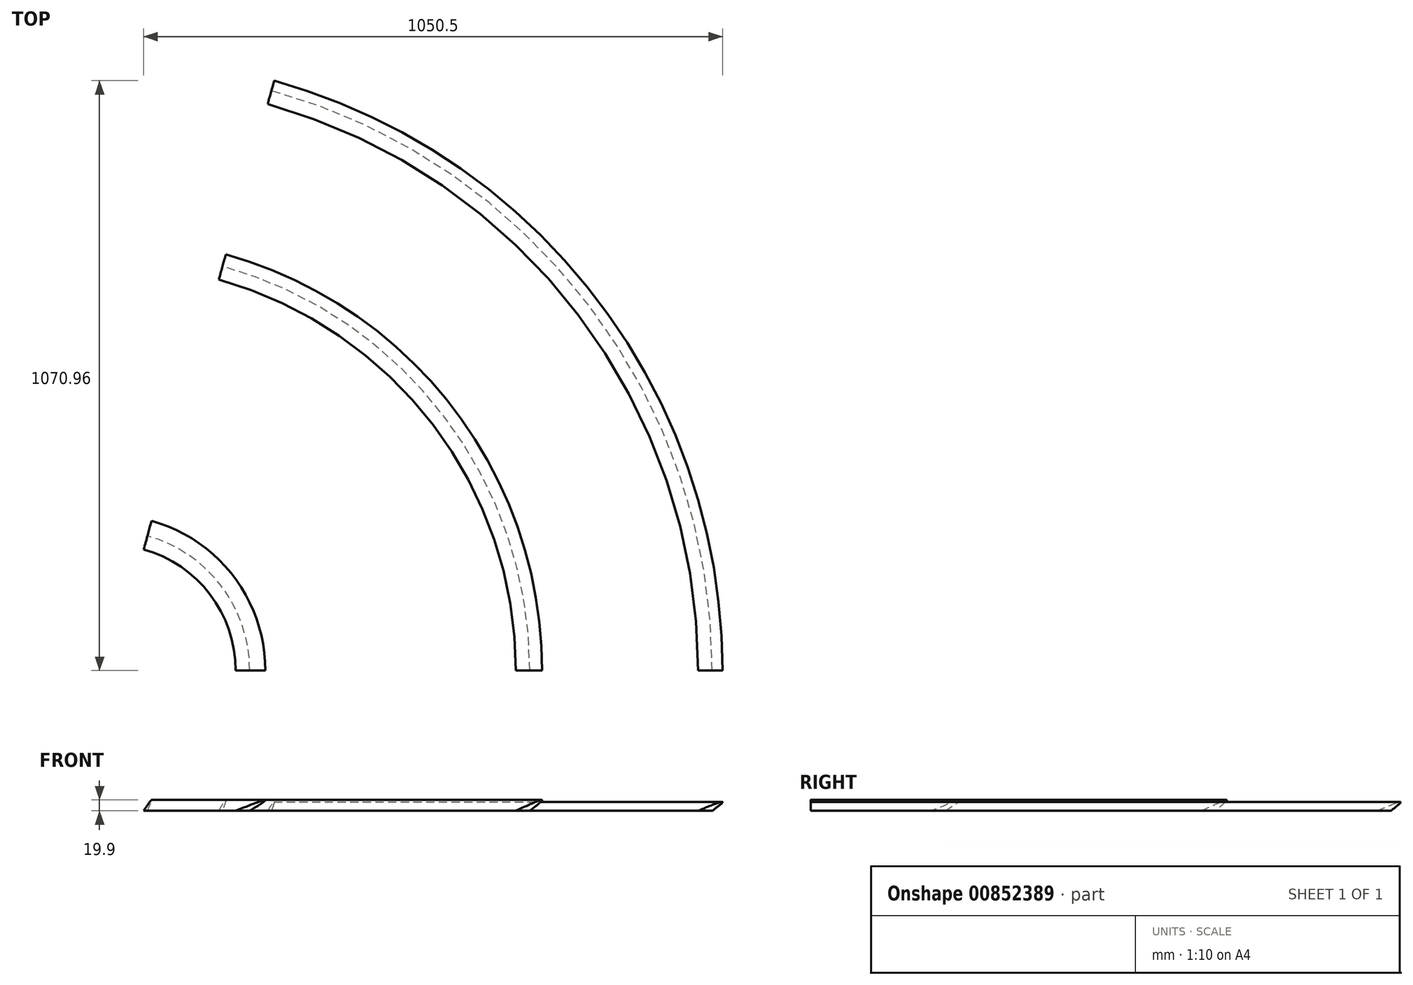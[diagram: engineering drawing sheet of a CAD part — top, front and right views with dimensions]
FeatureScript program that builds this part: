
annotation { "Feature Type Name" : "Feature", "Feature Type Description" : "" }
export const myFeature = defineFeature(function(context is Context, id is Id, definition is map)
    precondition{}
    {
        {
            var Q0;
            Q0=qCreatedBy(makeId("Top.planeOp"),FACE);
            var sketch = newSketch(context, id + "F0", { "sketchPlane" : qUnion([Q0])});
            skArc(sketch, "E0", {"start": v(1092.2, 0) * mm, "mid": v(869.68, 660.72) * mm, "end": v(292.8, 1052.22) * mm});
            skSolve(sketch);
        }
        {
            var Q0;
            Q0=qCreatedBy(makeId("Front.planeOp"),FACE);
            var sketch = newSketch(context, id + "F1", { "sketchPlane" : qUnion([Q0])});
            skLineSegment(sketch, "E1", {"start": v(253.65, 0) * mm, "end": v(228.12, 0) * mm});
            skFitSpline(sketch, "E2", {"points": [v(253.65, 0) * mm, v(281.93, 19.48) * mm, v(228.12, 0) * mm], "startDerivative": vector(99.78, 61.9) * mm, "endDerivative": vector(-140.66, -56.87) * mm});
            skSolve(sketch);
        }
        {
            var Q0;
            Q0=makeQuery(id+"F1.imprint","IMPRINT",FACE,{"disambiguationData":[TD([[makeQuery(id+"F1.imprint","IMPRINT",EDGE,{"derivedFrom":sQuery(id+"F1.wireOp",EDGE,"E1")}),-1.0]])]});
            var Q1;
            Q1=sQuery(id+"F0.wireOp",EDGE,"E0");
            sweep(context, id + "F2", {"profiles" : qUnion([Q0]), "path" : qUnion([Q1])});
        }
        {
            var Q0;
            Q0=qCreatedBy(makeId("Front.planeOp"),FACE);
            var sketch = newSketch(context, id + "F3", { "sketchPlane" : qUnion([Q0])});
            skLineSegment(sketch, "E3", {"start": v(761.9, 0) * mm, "end": v(736.58, 0) * mm});
            skFitSpline(sketch, "E4", {"points": [v(736.58, 0) * mm, v(784.22, 19.65) * mm, v(761.9, 0) * mm], "startDerivative": vector(122.33, 57.33) * mm, "endDerivative": vector(-80.96, -62.8) * mm});
            skSolve(sketch);
        }
        {
            var Q0;
            Q0=makeQuery(id+"F3.imprint","IMPRINT",FACE,{"disambiguationData":[TD([[makeQuery(id+"F3.imprint","IMPRINT",EDGE,{"derivedFrom":sQuery(id+"F3.wireOp",EDGE,"E3")}),-1.0]])]});
            var Q1;
            Q1=sQuery(id+"F0.wireOp",EDGE,"E0");
            sweep(context, id + "F4", {"profiles" : qUnion([Q0]), "path" : qUnion([Q1])});
        }
        {
            var Q0;
            Q0=qCreatedBy(makeId("Front.planeOp"),FACE);
            var sketch = newSketch(context, id + "F5", { "sketchPlane" : qUnion([Q0])});
            skLineSegment(sketch, "E5", {"start": v(1093.07, 0) * mm, "end": v(1067.42, 0) * mm});
            skFitSpline(sketch, "E6", {"points": [v(1067.42, 0) * mm, v(1111.6, 16.1) * mm, v(1093.07, 0) * mm], "startDerivative": vector(111, 46.94) * mm, "endDerivative": vector(-69.38, -52.26) * mm});
            skSolve(sketch);
        }
        {
            var Q0;
            Q0=makeQuery(id+"F5.imprint","IMPRINT",FACE,{"disambiguationData":[TD([[makeQuery(id+"F5.imprint","IMPRINT",EDGE,{"derivedFrom":sQuery(id+"F5.wireOp",EDGE,"E5")}),-1.0]])]});
            var Q1;
            Q1=sQuery(id+"F0.wireOp",EDGE,"E0");
            sweep(context, id + "F6", {"profiles" : qUnion([Q0]), "path" : qUnion([Q1])});
        }
    });
